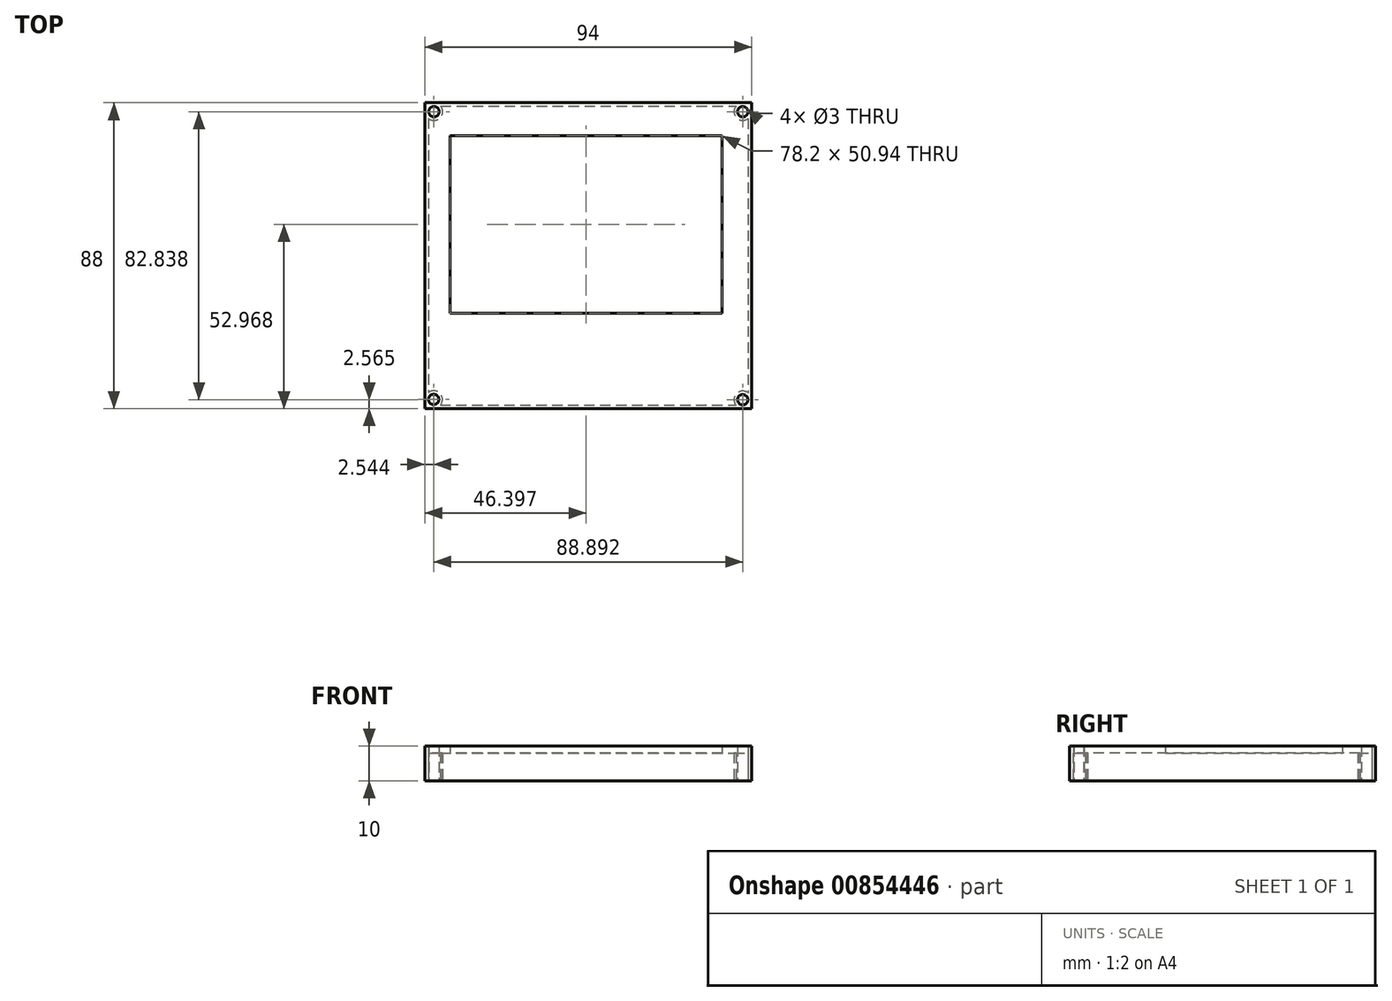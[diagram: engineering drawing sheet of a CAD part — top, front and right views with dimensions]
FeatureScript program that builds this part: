
annotation { "Feature Type Name" : "Feature", "Feature Type Description" : "" }
export const myFeature = defineFeature(function(context is Context, id is Id, definition is map)
    precondition{}
    {
        {
            var Q0;
            Q0=qCreatedBy(makeId("Top.planeOp"),FACE);
            var sketch = newSketch(context, id + "F0", { "sketchPlane" : qUnion([Q0])});
            skLineSegment(sketch, "E0.bottom", {"start": v(-40.36, 52.7) * mm, "end": v(53.64, 52.7) * mm});
            skLineSegment(sketch, "E0.top", {"start": v(-40.36, -35.3) * mm, "end": v(53.64, -35.3) * mm});
            skLineSegment(sketch, "E0.left", {"start": v(-40.36, 52.7) * mm, "end": v(-40.36, -35.3) * mm});
            skLineSegment(sketch, "E0.right", {"start": v(53.64, 52.7) * mm, "end": v(53.64, -35.3) * mm});
            skCircle(sketch, "E1", {"center": v(-37.75, 50.11) * mm, "radius": 2.5 * mm});
            skCircle(sketch, "E2", {"center": v(-37.82, -32.62) * mm, "radius": 2.5 * mm});
            skCircle(sketch, "E3", {"center": v(51.08, -32.72) * mm, "radius": 2.5 * mm});
            skCircle(sketch, "E4", {"center": v(51.08, 50.11) * mm, "radius": 2.5 * mm});
            skCircle(sketch, "E5", {"center": v(-37.75, 50.11) * mm, "radius": 1.5 * mm});
            skCircle(sketch, "E6", {"center": v(51.08, 50.11) * mm, "radius": 1.5 * mm});
            skCircle(sketch, "E7", {"center": v(51.08, -32.72) * mm, "radius": 1.5 * mm});
            skCircle(sketch, "E8", {"center": v(-37.82, -32.62) * mm, "radius": 1.5 * mm});
            skSolve(sketch);
        }
        {
            var Q0;
            Q0 = qSketchRegion(id + "F0", true);
            extrude(context, id + "F1", {"entities" : qUnion([Q0]), "depth" : 10 * mm, "offsetDistance" : 25 * mm});
        }
        {
            var Q0;
            Q0=qCreatedBy(makeId("Top.planeOp"),FACE);
            var sketch = newSketch(context, id + "F2", { "sketchPlane" : qUnion([Q0])});
            skLineSegment(sketch, "E9.bottom", {"start": v(-39.36, 51.7) * mm, "end": v(52.64, 51.7) * mm});
            skLineSegment(sketch, "E9.top", {"start": v(-39.36, -34.3) * mm, "end": v(52.64, -34.3) * mm});
            skLineSegment(sketch, "E9.left", {"start": v(-39.36, 51.7) * mm, "end": v(-39.36, -34.3) * mm});
            skLineSegment(sketch, "E9.right", {"start": v(52.64, 51.7) * mm, "end": v(52.64, -34.3) * mm});
            skSolve(sketch);
        }
        {
            var Q0;
            Q0 = qSketchRegion(id + "F2", true);
            extrude(context, id + "F3", {"entities" : qUnion([Q0]), "operationType" : NewBodyOperationType.REMOVE, "depth" : 8 * mm, "offsetDistance" : 25 * mm});
        }
        {
            var Q0;
            Q0=qCreatedBy(makeId("Top.planeOp"),FACE);
            var sketch = newSketch(context, id + "F4", { "sketchPlane" : qUnion([Q0])});
            skLineSegment(sketch, "E10.bottom", {"start": v(-33.06, 43.15) * mm, "end": v(45.14, 43.15) * mm});
            skLineSegment(sketch, "E10.top", {"start": v(-33.06, -7.8) * mm, "end": v(45.14, -7.8) * mm});
            skLineSegment(sketch, "E10.left", {"start": v(-33.06, 43.15) * mm, "end": v(-33.06, -7.8) * mm});
            skLineSegment(sketch, "E10.right", {"start": v(45.14, 43.15) * mm, "end": v(45.14, -7.8) * mm});
            skSolve(sketch);
        }
        {
            var Q0;
            Q0 = qSketchRegion(id + "F4", true);
            extrude(context, id + "F5", {"entities" : qUnion([Q0]), "operationType" : NewBodyOperationType.REMOVE, "depth" : 25 * mm, "offsetDistance" : 25 * mm});
        }
        {
            var Q0;
            Q0=makeQuery(id+"F0.imprint","IMPRINT",FACE,{"disambiguationData":[TD([[makeQuery(id+"F0.imprint","IMPRINT",EDGE,{"derivedFrom":sQuery(id+"F0.wireOp",EDGE,"E2")}),1.0]])]});
            var Q1;
            Q1=makeQuery(id+"F0.imprint","IMPRINT",FACE,{"disambiguationData":[TD([[makeQuery(id+"F0.imprint","IMPRINT",EDGE,{"derivedFrom":sQuery(id+"F0.wireOp",EDGE,"E1")}),1.0]])]});
            var Q2;
            Q2=makeQuery(id+"F0.imprint","IMPRINT",FACE,{"disambiguationData":[TD([[makeQuery(id+"F0.imprint","IMPRINT",EDGE,{"derivedFrom":sQuery(id+"F0.wireOp",EDGE,"E4")}),1.0]])]});
            var Q3;
            Q3=makeQuery(id+"F0.imprint","IMPRINT",FACE,{"disambiguationData":[TD([[makeQuery(id+"F0.imprint","IMPRINT",EDGE,{"derivedFrom":sQuery(id+"F0.wireOp",EDGE,"E3")}),1.0]])]});
            extrude(context, id + "F6", {"entities" : qUnion([Q0, Q1, Q2, Q3]), "operationType" : NewBodyOperationType.ADD, "depth" : 10 * mm, "offsetDistance" : 25 * mm});
        }
    });
